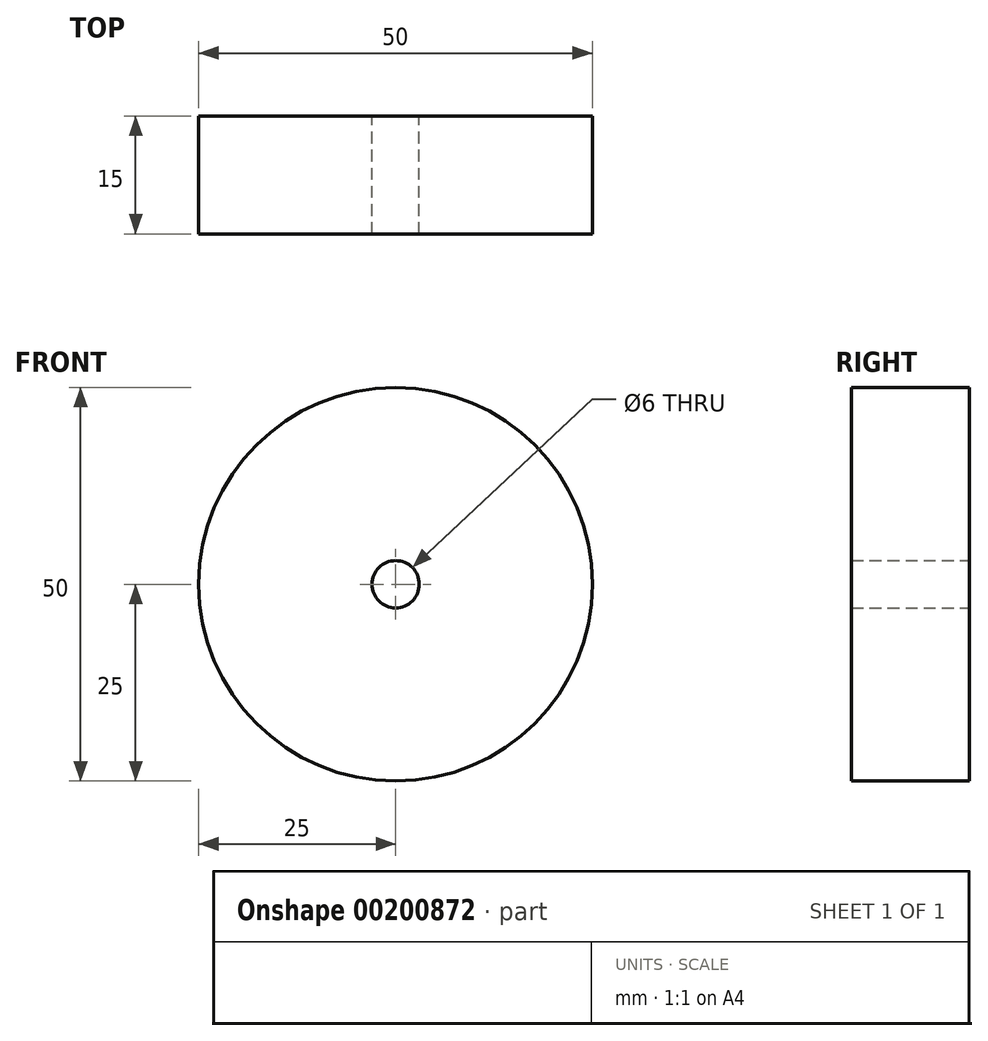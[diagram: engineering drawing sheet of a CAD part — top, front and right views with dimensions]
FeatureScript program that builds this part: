
annotation { "Feature Type Name" : "Feature", "Feature Type Description" : "" }
export const myFeature = defineFeature(function(context is Context, id is Id, definition is map)
    precondition{}
    {
        {
            var Q0;
            Q0=qCreatedBy(makeId("Front.planeOp"),FACE);
            var sketch = newSketch(context, id + "F0", { "sketchPlane" : qUnion([Q0])});
            skCircle(sketch, "E0", {"center": v(0, 0) * mm, "radius": 25 * mm});
            skCircle(sketch, "E1", {"center": v(0, 0) * mm, "radius": 3 * mm});
            skSolve(sketch);
        }
        {
            var Q0;
            Q0=makeQuery(id+"F0.imprint","IMPRINT",FACE,{"disambiguationData":[TD([[makeQuery(id+"F0.imprint","IMPRINT",EDGE,{"derivedFrom":sQuery(id+"F0.wireOp",EDGE,"E0")}),1.0]])]});
            extrude(context, id + "F1", {"entities" : qUnion([Q0]), "depth" : 15 * mm});
        }
    });
